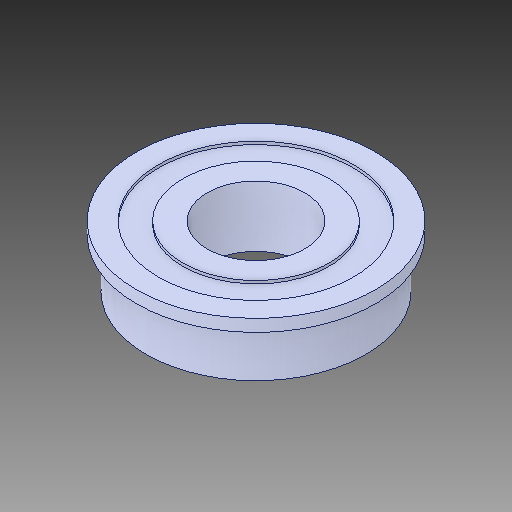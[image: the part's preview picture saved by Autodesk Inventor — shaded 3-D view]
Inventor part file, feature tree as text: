
AUTODESK INVENTOR PART (.ipt)
format: ipt  version: 2019 (Build 230136000, 136)  size: 123,904 bytes
history: native  units: in
note: dims shown in document units (in); Inventor stores cm internally (conversion verified against a paired STEP export)
features: revolve x1
ambient origin geometry x8: Origin, YZ Plane, XZ Plane, XY Plane, X Axis, Y Axis, Z Axis, Center Point
bodies: Solid1 (feature_tree)
feature tree (1):
  revolve  "Revolve1"  [1 undecoded]
note: 1 required parameter value undecoded (feature->parameter linkage not recoverable at this tier; creation-order binding heuristic only, values carry confidence <= 0.55)
